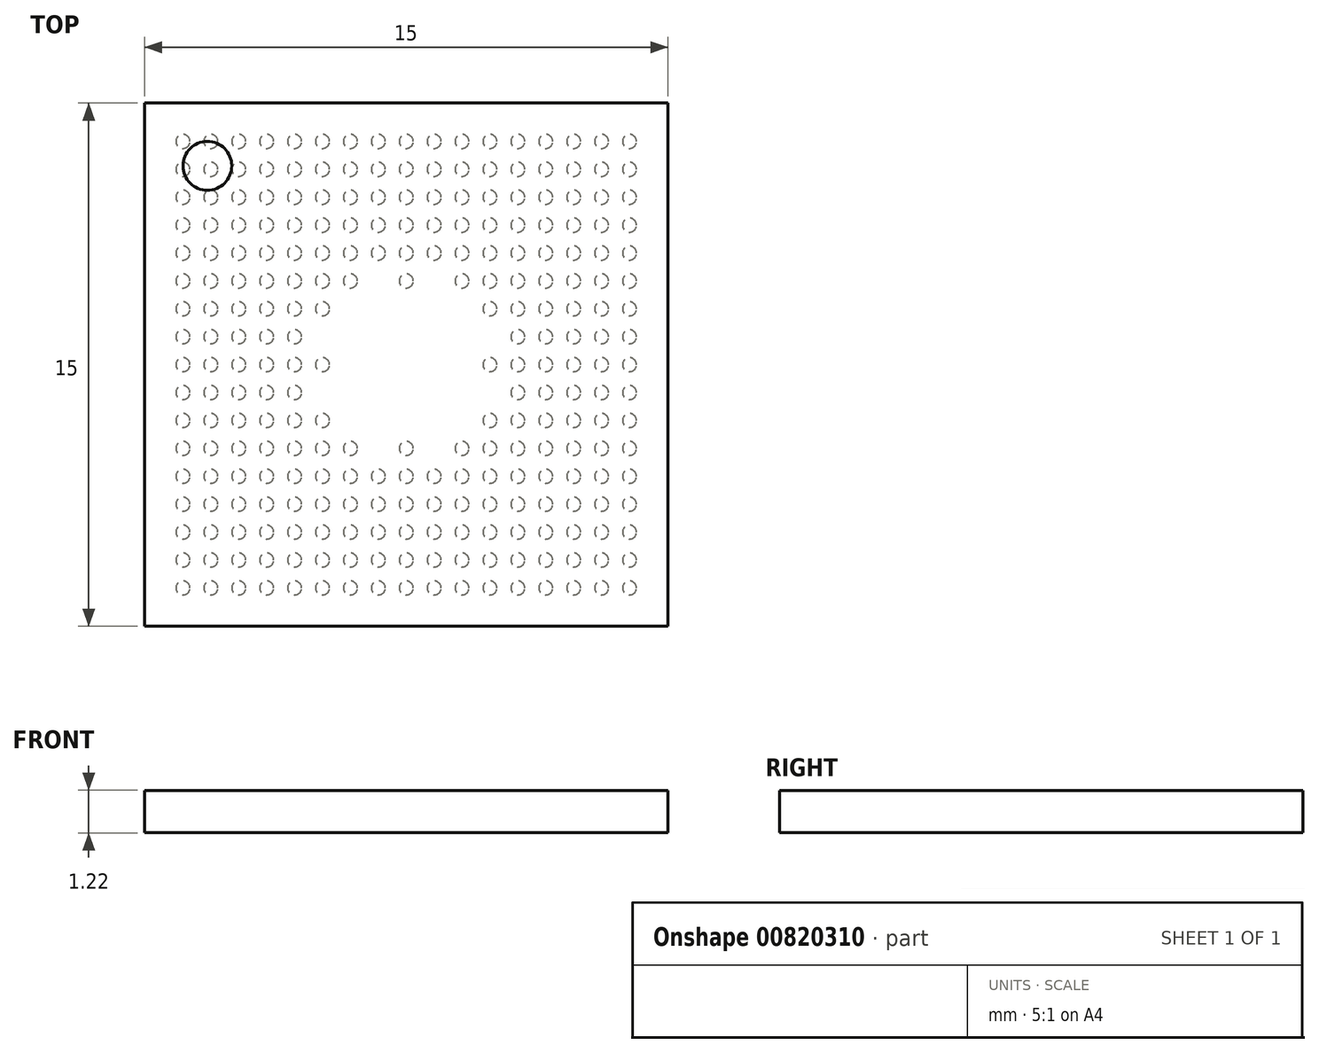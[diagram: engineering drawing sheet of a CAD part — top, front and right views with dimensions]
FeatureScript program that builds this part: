
annotation { "Feature Type Name" : "Feature", "Feature Type Description" : "" }
export const myFeature = defineFeature(function(context is Context, id is Id, definition is map)
    precondition{}
    {
        {
            var Q0;
            Q0=qCreatedBy(makeId("Top.planeOp"),FACE);
            var sketch = newSketch(context, id + "F0", { "sketchPlane" : qUnion([Q0])});
            skLineSegment(sketch, "E0.bottom", {"start": v(7.5, 7.5) * mm, "end": v(-7.5, 7.5) * mm});
            skLineSegment(sketch, "E0.top", {"start": v(7.5, -7.5) * mm, "end": v(-7.5, -7.5) * mm});
            skLineSegment(sketch, "E0.left", {"start": v(7.5, 7.5) * mm, "end": v(7.5, -7.5) * mm});
            skLineSegment(sketch, "E0.right", {"start": v(-7.5, 7.5) * mm, "end": v(-7.5, -7.5) * mm});
            skPoint(sketch, "E0.middle", {"position": v(0, 0) * mm});
            skSolve(sketch);
        }
        {
            var Q0;
            Q0=makeQuery(id+"F0.imprint","IMPRINT",FACE,{"disambiguationData":[TD([[makeQuery(id+"F0.imprint","IMPRINT",EDGE,{"derivedFrom":sQuery(id+"F0.wireOp",EDGE,"E0.bottom")}),1.0]])]});
            extrude(context, id + "F1", {"entities" : qUnion([Q0]), "depth" : 1.2 * mm, "offsetDistance" : 25 * mm});
        }
        {
            var Q0;
            Q0=makeQuery(id+"F1.opExtrude","CAP_FACE",FACE,{"disambiguationData":[OSD([sQuery(id+"F0.wireOp",EDGE,"E0.bottom"),sQuery(id+"F0.wireOp",EDGE,"E0.top"),sQuery(id+"F0.wireOp",EDGE,"E0.left"),sQuery(id+"F0.wireOp",EDGE,"E0.right")])],"isStart":false});
            var sketch = newSketch(context, id + "F2", { "sketchPlane" : qUnion([Q0])});
            skCircle(sketch, "E1", {"center": v(-5.7, 5.7) * mm, "radius": 0.7 * mm});
            skSolve(sketch);
        }
        {
            var Q0;
            Q0=makeQuery(id+"F2.imprint","IMPRINT",FACE,{"disambiguationData":[TD([[makeQuery(id+"F2.imprint","IMPRINT",EDGE,{"derivedFrom":sQuery(id+"F2.wireOp",EDGE,"E1")}),1.0]])]});
            extrude(context, id + "F3", {"entities" : qUnion([Q0]), "endBound" : BoundingType.SYMMETRIC, "depth" : 0.01 * mm, "offsetDistance" : 25 * mm});
        }
        {
            var Q0;
            Q0=makeQuery(id+"F0.imprint","IMPRINT",FACE,{"disambiguationData":[TD([[makeQuery(id+"F0.imprint","IMPRINT",EDGE,{"derivedFrom":sQuery(id+"F0.wireOp",EDGE,"E0.bottom")}),1.0]])]});
            var sketch = newSketch(context, id + "F4", { "sketchPlane" : qUnion([Q0])});
            skCircle(sketch, "E2", {"center": v(0, 0) * mm, "radius": 0.2 * mm});
            skCircle(sketch, "E3", {"center": v(0, -0.8) * mm, "radius": 0.2 * mm});
            skCircle(sketch, "E4", {"center": v(0.8, 0) * mm, "radius": 0.2 * mm});
            skCircle(sketch, "E5", {"center": v(0.8, -0.8) * mm, "radius": 0.2 * mm});
            skCircle(sketch, "E6", {"center": v(1.6, -0.8) * mm, "radius": 0.2 * mm});
            skCircle(sketch, "E7", {"center": v(2.4, -0.8) * mm, "radius": 0.2 * mm});
            skCircle(sketch, "E8", {"center": v(3.2, -0.8) * mm, "radius": 0.2 * mm});
            skCircle(sketch, "E9", {"center": v(4, -0.8) * mm, "radius": 0.2 * mm});
            skCircle(sketch, "E10", {"center": v(4.8, -0.8) * mm, "radius": 0.2 * mm});
            skCircle(sketch, "E11", {"center": v(5.6, -0.8) * mm, "radius": 0.2 * mm});
            skCircle(sketch, "E12", {"center": v(6.4, -0.8) * mm, "radius": 0.2 * mm});
            skCircle(sketch, "E13", {"center": v(1.6, 0) * mm, "radius": 0.2 * mm});
            skCircle(sketch, "E14", {"center": v(2.4, 0) * mm, "radius": 0.2 * mm});
            skCircle(sketch, "E15", {"center": v(3.2, 0) * mm, "radius": 0.2 * mm});
            skCircle(sketch, "E16", {"center": v(4, 0) * mm, "radius": 0.2 * mm});
            skCircle(sketch, "E17", {"center": v(4.8, 0) * mm, "radius": 0.2 * mm});
            skCircle(sketch, "E18", {"center": v(5.6, 0) * mm, "radius": 0.2 * mm});
            skCircle(sketch, "E19", {"center": v(6.4, 0) * mm, "radius": 0.2 * mm});
            skCircle(sketch, "E20.MirrorC", {"center": v(3.2, -1.6) * mm, "radius": 0.2 * mm});
            skCircle(sketch, "E21.MirrorC", {"center": v(2.4, -1.6) * mm, "radius": 0.2 * mm});
            skCircle(sketch, "E22.MirrorC", {"center": v(0.8, -1.6) * mm, "radius": 0.2 * mm});
            skCircle(sketch, "E23.MirrorC", {"center": v(1.6, -1.6) * mm, "radius": 0.2 * mm});
            skCircle(sketch, "E24.MirrorC", {"center": v(4, -1.6) * mm, "radius": 0.2 * mm});
            skCircle(sketch, "E25.MirrorC", {"center": v(0.8, -2.4) * mm, "radius": 0.2 * mm});
            skCircle(sketch, "E26.MirrorC", {"center": v(5.6, -1.6) * mm, "radius": 0.2 * mm});
            skCircle(sketch, "E27.MirrorC", {"center": v(0, -1.6) * mm, "radius": 0.2 * mm});
            skCircle(sketch, "E28.MirrorC", {"center": v(5.6, -2.4) * mm, "radius": 0.2 * mm});
            skCircle(sketch, "E29.MirrorC", {"center": v(0, -2.4) * mm, "radius": 0.2 * mm});
            skCircle(sketch, "E30.MirrorC", {"center": v(4.8, -1.6) * mm, "radius": 0.2 * mm});
            skCircle(sketch, "E31.MirrorC", {"center": v(2.4, -2.4) * mm, "radius": 0.2 * mm});
            skCircle(sketch, "E32.MirrorC", {"center": v(6.4, -1.6) * mm, "radius": 0.2 * mm});
            skCircle(sketch, "E33.MirrorC", {"center": v(1.6, -2.4) * mm, "radius": 0.2 * mm});
            skCircle(sketch, "E34.MirrorC", {"center": v(4.8, -2.4) * mm, "radius": 0.2 * mm});
            skCircle(sketch, "E35.MirrorC", {"center": v(4, -2.4) * mm, "radius": 0.2 * mm});
            skCircle(sketch, "E36.MirrorC", {"center": v(3.2, -2.4) * mm, "radius": 0.2 * mm});
            skCircle(sketch, "E37.MirrorC", {"center": v(6.4, -2.4) * mm, "radius": 0.2 * mm});
            skCircle(sketch, "E38.MirrorC", {"center": v(6.4, -4) * mm, "radius": 0.2 * mm});
            skCircle(sketch, "E39.MirrorC", {"center": v(5.6, -4) * mm, "radius": 0.2 * mm});
            skCircle(sketch, "E40.MirrorC", {"center": v(4.8, -4) * mm, "radius": 0.2 * mm});
            skCircle(sketch, "E41.MirrorC", {"center": v(2.4, -5.6) * mm, "radius": 0.2 * mm});
            skCircle(sketch, "E42.MirrorC", {"center": v(1.6, -5.6) * mm, "radius": 0.2 * mm});
            skCircle(sketch, "E43.MirrorC", {"center": v(3.2, -5.6) * mm, "radius": 0.2 * mm});
            skCircle(sketch, "E44.MirrorC", {"center": v(4, -5.6) * mm, "radius": 0.2 * mm});
            skCircle(sketch, "E45.MirrorC", {"center": v(4.8, -5.6) * mm, "radius": 0.2 * mm});
            skCircle(sketch, "E46.MirrorC", {"center": v(0, -5.6) * mm, "radius": 0.2 * mm});
            skCircle(sketch, "E47.MirrorC", {"center": v(1.6, -4) * mm, "radius": 0.2 * mm});
            skCircle(sketch, "E48.MirrorC", {"center": v(5.6, -5.6) * mm, "radius": 0.2 * mm});
            skCircle(sketch, "E49.MirrorC", {"center": v(0, -4.8) * mm, "radius": 0.2 * mm});
            skCircle(sketch, "E50.MirrorC", {"center": v(2.4, -4) * mm, "radius": 0.2 * mm});
            skCircle(sketch, "E51.MirrorC", {"center": v(4, -4) * mm, "radius": 0.2 * mm});
            skCircle(sketch, "E52.MirrorC", {"center": v(3.2, -4) * mm, "radius": 0.2 * mm});
            skCircle(sketch, "E53.MirrorC", {"center": v(0.8, -5.6) * mm, "radius": 0.2 * mm});
            skCircle(sketch, "E54.MirrorC", {"center": v(0, -4) * mm, "radius": 0.2 * mm});
            skCircle(sketch, "E55.MirrorC", {"center": v(0.8, -4.8) * mm, "radius": 0.2 * mm});
            skCircle(sketch, "E56.MirrorC", {"center": v(1.6, -4.8) * mm, "radius": 0.2 * mm});
            skCircle(sketch, "E57.MirrorC", {"center": v(2.4, -4.8) * mm, "radius": 0.2 * mm});
            skCircle(sketch, "E58.MirrorC", {"center": v(6.4, -5.6) * mm, "radius": 0.2 * mm});
            skCircle(sketch, "E59.MirrorC", {"center": v(0.8, -4) * mm, "radius": 0.2 * mm});
            skCircle(sketch, "E60.MirrorC", {"center": v(3.2, -4.8) * mm, "radius": 0.2 * mm});
            skCircle(sketch, "E61.MirrorC", {"center": v(6.4, -4.8) * mm, "radius": 0.2 * mm});
            skCircle(sketch, "E62.MirrorC", {"center": v(5.6, -4.8) * mm, "radius": 0.2 * mm});
            skCircle(sketch, "E63.MirrorC", {"center": v(4.8, -4.8) * mm, "radius": 0.2 * mm});
            skCircle(sketch, "E64.MirrorC", {"center": v(4, -4.8) * mm, "radius": 0.2 * mm});
            skCircle(sketch, "E65.MirrorC", {"center": v(0, -3.2) * mm, "radius": 0.2 * mm});
            skCircle(sketch, "E66.MirrorC", {"center": v(0.8, -3.2) * mm, "radius": 0.2 * mm});
            skCircle(sketch, "E67.MirrorC", {"center": v(1.6, -3.2) * mm, "radius": 0.2 * mm});
            skCircle(sketch, "E68.MirrorC", {"center": v(2.4, -3.2) * mm, "radius": 0.2 * mm});
            skCircle(sketch, "E69.MirrorC", {"center": v(3.2, -3.2) * mm, "radius": 0.2 * mm});
            skCircle(sketch, "E70.MirrorC", {"center": v(4, -3.2) * mm, "radius": 0.2 * mm});
            skCircle(sketch, "E71.MirrorC", {"center": v(4.8, -3.2) * mm, "radius": 0.2 * mm});
            skCircle(sketch, "E72.MirrorC", {"center": v(5.6, -3.2) * mm, "radius": 0.2 * mm});
            skCircle(sketch, "E73.MirrorC", {"center": v(6.4, -3.2) * mm, "radius": 0.2 * mm});
            skCircle(sketch, "E74.MirrorC", {"center": v(5.6, -6.4) * mm, "radius": 0.2 * mm});
            skCircle(sketch, "E75.MirrorC", {"center": v(0, -6.4) * mm, "radius": 0.2 * mm});
            skCircle(sketch, "E76.MirrorC", {"center": v(2.4, -6.4) * mm, "radius": 0.2 * mm});
            skCircle(sketch, "E77.MirrorC", {"center": v(1.6, -6.4) * mm, "radius": 0.2 * mm});
            skCircle(sketch, "E78.MirrorC", {"center": v(6.4, -6.4) * mm, "radius": 0.2 * mm});
            skCircle(sketch, "E79.MirrorC", {"center": v(3.2, -6.4) * mm, "radius": 0.2 * mm});
            skCircle(sketch, "E80.MirrorC", {"center": v(4.8, -6.4) * mm, "radius": 0.2 * mm});
            skCircle(sketch, "E81.MirrorC", {"center": v(0.8, -6.4) * mm, "radius": 0.2 * mm});
            skCircle(sketch, "E82.MirrorC", {"center": v(4, -6.4) * mm, "radius": 0.2 * mm});
            skCircle(sketch, "E83.MirrorC", {"center": v(-1.6, -4.8) * mm, "radius": 0.2 * mm});
            skCircle(sketch, "E84.MirrorC", {"center": v(-1.6, -2.4) * mm, "radius": 0.2 * mm});
            skCircle(sketch, "E85.MirrorC", {"center": v(-4, -1.6) * mm, "radius": 0.2 * mm});
            skCircle(sketch, "E86.MirrorC", {"center": v(-4.8, -4) * mm, "radius": 0.2 * mm});
            skCircle(sketch, "E87.MirrorC", {"center": v(-0.8, -6.4) * mm, "radius": 0.2 * mm});
            skCircle(sketch, "E88.MirrorC", {"center": v(-5.6, -3.2) * mm, "radius": 0.2 * mm});
            skCircle(sketch, "E89.MirrorC", {"center": v(-2.4, -4) * mm, "radius": 0.2 * mm});
            skCircle(sketch, "E90.MirrorC", {"center": v(-4.8, -2.4) * mm, "radius": 0.2 * mm});
            skCircle(sketch, "E91.MirrorC", {"center": v(-4.8, -3.2) * mm, "radius": 0.2 * mm});
            skCircle(sketch, "E92.MirrorC", {"center": v(-5.6, 0) * mm, "radius": 0.2 * mm});
            skCircle(sketch, "E93.MirrorC", {"center": v(-4.8, -6.4) * mm, "radius": 0.2 * mm});
            skCircle(sketch, "E94.MirrorC", {"center": v(-4, -4.8) * mm, "radius": 0.2 * mm});
            skCircle(sketch, "E95.MirrorC", {"center": v(-1.6, -1.6) * mm, "radius": 0.2 * mm});
            skCircle(sketch, "E96.MirrorC", {"center": v(-5.6, -4) * mm, "radius": 0.2 * mm});
            skCircle(sketch, "E97.MirrorC", {"center": v(-6.4, -1.6) * mm, "radius": 0.2 * mm});
            skCircle(sketch, "E98.MirrorC", {"center": v(-6.4, -3.2) * mm, "radius": 0.2 * mm});
            skCircle(sketch, "E99.MirrorC", {"center": v(-5.6, -1.6) * mm, "radius": 0.2 * mm});
            skCircle(sketch, "E100.MirrorC", {"center": v(-2.4, -5.6) * mm, "radius": 0.2 * mm});
            skCircle(sketch, "E101.MirrorC", {"center": v(-2.4, -4.8) * mm, "radius": 0.2 * mm});
            skCircle(sketch, "E102.MirrorC", {"center": v(-1.6, -3.2) * mm, "radius": 0.2 * mm});
            skCircle(sketch, "E103.MirrorC", {"center": v(-5.6, -6.4) * mm, "radius": 0.2 * mm});
            skCircle(sketch, "E104.MirrorC", {"center": v(-6.4, -5.6) * mm, "radius": 0.2 * mm});
            skCircle(sketch, "E105.MirrorC", {"center": v(-1.6, -5.6) * mm, "radius": 0.2 * mm});
            skCircle(sketch, "E106.MirrorC", {"center": v(-4, -4) * mm, "radius": 0.2 * mm});
            skCircle(sketch, "E107.MirrorC", {"center": v(-4, -2.4) * mm, "radius": 0.2 * mm});
            skCircle(sketch, "E108.MirrorC", {"center": v(-6.4, 0) * mm, "radius": 0.2 * mm});
            skCircle(sketch, "E109.MirrorC", {"center": v(-0.8, -4) * mm, "radius": 0.2 * mm});
            skCircle(sketch, "E110.MirrorC", {"center": v(-3.2, -5.6) * mm, "radius": 0.2 * mm});
            skCircle(sketch, "E111.MirrorC", {"center": v(-3.2, -4) * mm, "radius": 0.2 * mm});
            skCircle(sketch, "E112.MirrorC", {"center": v(-3.2, -2.4) * mm, "radius": 0.2 * mm});
            skCircle(sketch, "E113.MirrorC", {"center": v(-3.2, -1.6) * mm, "radius": 0.2 * mm});
            skCircle(sketch, "E114.MirrorC", {"center": v(-2.4, -3.2) * mm, "radius": 0.2 * mm});
            skCircle(sketch, "E115.MirrorC", {"center": v(-0.8, -3.2) * mm, "radius": 0.2 * mm});
            skCircle(sketch, "E116.MirrorC", {"center": v(-5.6, -2.4) * mm, "radius": 0.2 * mm});
            skCircle(sketch, "E117.MirrorC", {"center": v(-2.4, -6.4) * mm, "radius": 0.2 * mm});
            skCircle(sketch, "E118.MirrorC", {"center": v(-4, -5.6) * mm, "radius": 0.2 * mm});
            skCircle(sketch, "E119.MirrorC", {"center": v(-3.2, -4.8) * mm, "radius": 0.2 * mm});
            skCircle(sketch, "E120.MirrorC", {"center": v(-0.8, -5.6) * mm, "radius": 0.2 * mm});
            skCircle(sketch, "E121.MirrorC", {"center": v(-6.4, -2.4) * mm, "radius": 0.2 * mm});
            skCircle(sketch, "E122.MirrorC", {"center": v(-2.4, -1.6) * mm, "radius": 0.2 * mm});
            skCircle(sketch, "E123.MirrorC", {"center": v(-3.2, -3.2) * mm, "radius": 0.2 * mm});
            skCircle(sketch, "E124.MirrorC", {"center": v(-6.4, -6.4) * mm, "radius": 0.2 * mm});
            skCircle(sketch, "E125.MirrorC", {"center": v(-0.8, -4.8) * mm, "radius": 0.2 * mm});
            skCircle(sketch, "E126.MirrorC", {"center": v(-4, 0) * mm, "radius": 0.2 * mm});
            skCircle(sketch, "E127.MirrorC", {"center": v(-5.6, -4.8) * mm, "radius": 0.2 * mm});
            skCircle(sketch, "E128.MirrorC", {"center": v(-4.8, -1.6) * mm, "radius": 0.2 * mm});
            skCircle(sketch, "E129.MirrorC", {"center": v(-4.8, 0) * mm, "radius": 0.2 * mm});
            skCircle(sketch, "E130.MirrorC", {"center": v(-4.8, -0.8) * mm, "radius": 0.2 * mm});
            skCircle(sketch, "E131.MirrorC", {"center": v(-5.6, -0.8) * mm, "radius": 0.2 * mm});
            skCircle(sketch, "E132.MirrorC", {"center": v(-0.8, -2.4) * mm, "radius": 0.2 * mm});
            skCircle(sketch, "E133.MirrorC", {"center": v(-6.4, -4.8) * mm, "radius": 0.2 * mm});
            skCircle(sketch, "E134.MirrorC", {"center": v(-4, -0.8) * mm, "radius": 0.2 * mm});
            skCircle(sketch, "E135.MirrorC", {"center": v(-6.4, -0.8) * mm, "radius": 0.2 * mm});
            skCircle(sketch, "E136.MirrorC", {"center": v(-5.6, -5.6) * mm, "radius": 0.2 * mm});
            skCircle(sketch, "E137.MirrorC", {"center": v(-1.6, -4) * mm, "radius": 0.2 * mm});
            skCircle(sketch, "E138.MirrorC", {"center": v(-3.2, -0.8) * mm, "radius": 0.2 * mm});
            skCircle(sketch, "E139.MirrorC", {"center": v(-2.4, -0.8) * mm, "radius": 0.2 * mm});
            skCircle(sketch, "E140.MirrorC", {"center": v(-4.8, -5.6) * mm, "radius": 0.2 * mm});
            skCircle(sketch, "E141.MirrorC", {"center": v(-0.8, -0.8) * mm, "radius": 0.2 * mm});
            skCircle(sketch, "E142.MirrorC", {"center": v(-1.6, -0.8) * mm, "radius": 0.2 * mm});
            skCircle(sketch, "E143.MirrorC", {"center": v(-1.6, -6.4) * mm, "radius": 0.2 * mm});
            skCircle(sketch, "E144.MirrorC", {"center": v(-0.8, 0) * mm, "radius": 0.2 * mm});
            skCircle(sketch, "E145.MirrorC", {"center": v(-2.4, -2.4) * mm, "radius": 0.2 * mm});
            skCircle(sketch, "E146.MirrorC", {"center": v(-6.4, -4) * mm, "radius": 0.2 * mm});
            skCircle(sketch, "E147.MirrorC", {"center": v(-0.8, -1.6) * mm, "radius": 0.2 * mm});
            skCircle(sketch, "E148.MirrorC", {"center": v(-4, -6.4) * mm, "radius": 0.2 * mm});
            skCircle(sketch, "E149.MirrorC", {"center": v(-4, -3.2) * mm, "radius": 0.2 * mm});
            skCircle(sketch, "E150.MirrorC", {"center": v(-1.6, 0) * mm, "radius": 0.2 * mm});
            skCircle(sketch, "E151.MirrorC", {"center": v(-3.2, 0) * mm, "radius": 0.2 * mm});
            skCircle(sketch, "E152.MirrorC", {"center": v(-2.4, 0) * mm, "radius": 0.2 * mm});
            skCircle(sketch, "E153.MirrorC", {"center": v(-4.8, -4.8) * mm, "radius": 0.2 * mm});
            skCircle(sketch, "E154.MirrorC", {"center": v(-3.2, -6.4) * mm, "radius": 0.2 * mm});
            skCircle(sketch, "E155.MirrorC", {"center": v(0, 4) * mm, "radius": 0.2 * mm});
            skCircle(sketch, "E156.MirrorC", {"center": v(0, 4.8) * mm, "radius": 0.2 * mm});
            skCircle(sketch, "E157.MirrorC", {"center": v(0, 5.6) * mm, "radius": 0.2 * mm});
            skCircle(sketch, "E158.MirrorC", {"center": v(0, 0.8) * mm, "radius": 0.2 * mm});
            skCircle(sketch, "E159.MirrorC", {"center": v(0, 6.4) * mm, "radius": 0.2 * mm});
            skCircle(sketch, "E160.MirrorC", {"center": v(0, 1.6) * mm, "radius": 0.2 * mm});
            skCircle(sketch, "E161.MirrorC", {"center": v(0, 3.2) * mm, "radius": 0.2 * mm});
            skCircle(sketch, "E162.MirrorC", {"center": v(0, 2.4) * mm, "radius": 0.2 * mm});
            skCircle(sketch, "E163.MirrorC", {"center": v(4.8, 3.2) * mm, "radius": 0.2 * mm});
            skCircle(sketch, "E164.MirrorC", {"center": v(-4.8, 4) * mm, "radius": 0.2 * mm});
            skCircle(sketch, "E165.MirrorC", {"center": v(-2.4, 4.8) * mm, "radius": 0.2 * mm});
            skCircle(sketch, "E166.MirrorC", {"center": v(-0.8, 3.2) * mm, "radius": 0.2 * mm});
            skCircle(sketch, "E167.MirrorC", {"center": v(1.6, 1.6) * mm, "radius": 0.2 * mm});
            skCircle(sketch, "E168.MirrorC", {"center": v(5.6, 4) * mm, "radius": 0.2 * mm});
            skCircle(sketch, "E169.MirrorC", {"center": v(0.8, 4.8) * mm, "radius": 0.2 * mm});
            skCircle(sketch, "E170.MirrorC", {"center": v(-4.8, 1.6) * mm, "radius": 0.2 * mm});
            skCircle(sketch, "E171.MirrorC", {"center": v(4, 3.2) * mm, "radius": 0.2 * mm});
            skCircle(sketch, "E172.MirrorC", {"center": v(-4, 1.6) * mm, "radius": 0.2 * mm});
            skCircle(sketch, "E173.MirrorC", {"center": v(-2.4, 5.6) * mm, "radius": 0.2 * mm});
            skCircle(sketch, "E174.MirrorC", {"center": v(-2.4, 3.2) * mm, "radius": 0.2 * mm});
            skCircle(sketch, "E175.MirrorC", {"center": v(0.8, 1.6) * mm, "radius": 0.2 * mm});
            skCircle(sketch, "E176.MirrorC", {"center": v(6.4, 4) * mm, "radius": 0.2 * mm});
            skCircle(sketch, "E177.MirrorC", {"center": v(6.4, 0.8) * mm, "radius": 0.2 * mm});
            skCircle(sketch, "E178.MirrorC", {"center": v(5.6, 0.8) * mm, "radius": 0.2 * mm});
            skCircle(sketch, "E179.MirrorC", {"center": v(4.8, 0.8) * mm, "radius": 0.2 * mm});
            skCircle(sketch, "E180.MirrorC", {"center": v(4, 0.8) * mm, "radius": 0.2 * mm});
            skCircle(sketch, "E181.MirrorC", {"center": v(3.2, 0.8) * mm, "radius": 0.2 * mm});
            skCircle(sketch, "E182.MirrorC", {"center": v(2.4, 0.8) * mm, "radius": 0.2 * mm});
            skCircle(sketch, "E183.MirrorC", {"center": v(1.6, 0.8) * mm, "radius": 0.2 * mm});
            skCircle(sketch, "E184.MirrorC", {"center": v(0.8, 0.8) * mm, "radius": 0.2 * mm});
            skCircle(sketch, "E185.MirrorC", {"center": v(-5.6, 4.8) * mm, "radius": 0.2 * mm});
            skCircle(sketch, "E186.MirrorC", {"center": v(-1.6, 6.4) * mm, "radius": 0.2 * mm});
            skCircle(sketch, "E187.MirrorC", {"center": v(3.2, 3.2) * mm, "radius": 0.2 * mm});
            skCircle(sketch, "E188.MirrorC", {"center": v(-1.6, 2.4) * mm, "radius": 0.2 * mm});
            skCircle(sketch, "E189.MirrorC", {"center": v(-5.6, 1.6) * mm, "radius": 0.2 * mm});
            skCircle(sketch, "E190.MirrorC", {"center": v(-3.2, 1.6) * mm, "radius": 0.2 * mm});
            skCircle(sketch, "E191.MirrorC", {"center": v(2.4, 1.6) * mm, "radius": 0.2 * mm});
            skCircle(sketch, "E192.MirrorC", {"center": v(6.4, 2.4) * mm, "radius": 0.2 * mm});
            skCircle(sketch, "E193.MirrorC", {"center": v(0.8, 5.6) * mm, "radius": 0.2 * mm});
            skCircle(sketch, "E194.MirrorC", {"center": v(2.4, 3.2) * mm, "radius": 0.2 * mm});
            skCircle(sketch, "E195.MirrorC", {"center": v(-1.6, 4.8) * mm, "radius": 0.2 * mm});
            skCircle(sketch, "E196.MirrorC", {"center": v(-6.4, 3.2) * mm, "radius": 0.2 * mm});
            skCircle(sketch, "E197.MirrorC", {"center": v(-3.2, 2.4) * mm, "radius": 0.2 * mm});
            skCircle(sketch, "E198.MirrorC", {"center": v(3.2, 1.6) * mm, "radius": 0.2 * mm});
            skCircle(sketch, "E199.MirrorC", {"center": v(3.2, 2.4) * mm, "radius": 0.2 * mm});
            skCircle(sketch, "E200.MirrorC", {"center": v(3.2, 4) * mm, "radius": 0.2 * mm});
            skCircle(sketch, "E201.MirrorC", {"center": v(-1.6, 0.8) * mm, "radius": 0.2 * mm});
            skCircle(sketch, "E202.MirrorC", {"center": v(4, 2.4) * mm, "radius": 0.2 * mm});
            skCircle(sketch, "E203.MirrorC", {"center": v(4, 4) * mm, "radius": 0.2 * mm});
            skCircle(sketch, "E204.MirrorC", {"center": v(-0.8, 0.8) * mm, "radius": 0.2 * mm});
            skCircle(sketch, "E205.MirrorC", {"center": v(-3.2, 6.4) * mm, "radius": 0.2 * mm});
            skCircle(sketch, "E206.MirrorC", {"center": v(1.6, 3.2) * mm, "radius": 0.2 * mm});
            skCircle(sketch, "E207.MirrorC", {"center": v(-6.4, 1.6) * mm, "radius": 0.2 * mm});
            skCircle(sketch, "E208.MirrorC", {"center": v(-3.2, 4) * mm, "radius": 0.2 * mm});
            skCircle(sketch, "E209.MirrorC", {"center": v(-4.8, 5.6) * mm, "radius": 0.2 * mm});
            skCircle(sketch, "E210.MirrorC", {"center": v(-4.8, 4.8) * mm, "radius": 0.2 * mm});
            skCircle(sketch, "E211.MirrorC", {"center": v(0.8, 3.2) * mm, "radius": 0.2 * mm});
            skCircle(sketch, "E212.MirrorC", {"center": v(4, 6.4) * mm, "radius": 0.2 * mm});
            skCircle(sketch, "E213.MirrorC", {"center": v(-5.6, 4) * mm, "radius": 0.2 * mm});
            skCircle(sketch, "E214.MirrorC", {"center": v(-3.2, 5.6) * mm, "radius": 0.2 * mm});
            skCircle(sketch, "E215.MirrorC", {"center": v(4.8, 2.4) * mm, "radius": 0.2 * mm});
            skCircle(sketch, "E216.MirrorC", {"center": v(-0.8, 4.8) * mm, "radius": 0.2 * mm});
            skCircle(sketch, "E217.MirrorC", {"center": v(-2.4, 0.8) * mm, "radius": 0.2 * mm});
            skCircle(sketch, "E218.MirrorC", {"center": v(2.4, 4) * mm, "radius": 0.2 * mm});
            skCircle(sketch, "E219.MirrorC", {"center": v(-4.8, 3.2) * mm, "radius": 0.2 * mm});
            skCircle(sketch, "E220.MirrorC", {"center": v(1.6, 2.4) * mm, "radius": 0.2 * mm});
            skCircle(sketch, "E221.MirrorC", {"center": v(1.6, 6.4) * mm, "radius": 0.2 * mm});
            skCircle(sketch, "E222.MirrorC", {"center": v(6.4, 4.8) * mm, "radius": 0.2 * mm});
            skCircle(sketch, "E223.MirrorC", {"center": v(-4, 6.4) * mm, "radius": 0.2 * mm});
            skCircle(sketch, "E224.MirrorC", {"center": v(4.8, 5.6) * mm, "radius": 0.2 * mm});
            skCircle(sketch, "E225.MirrorC", {"center": v(-4, 4) * mm, "radius": 0.2 * mm});
            skCircle(sketch, "E226.MirrorC", {"center": v(-0.8, 5.6) * mm, "radius": 0.2 * mm});
            skCircle(sketch, "E227.MirrorC", {"center": v(-4, 0.8) * mm, "radius": 0.2 * mm});
            skCircle(sketch, "E228.MirrorC", {"center": v(-3.2, 0.8) * mm, "radius": 0.2 * mm});
            skCircle(sketch, "E229.MirrorC", {"center": v(-6.4, 6.4) * mm, "radius": 0.2 * mm});
            skCircle(sketch, "E230.MirrorC", {"center": v(-0.8, 1.6) * mm, "radius": 0.2 * mm});
            skCircle(sketch, "E231.MirrorC", {"center": v(4, 4.8) * mm, "radius": 0.2 * mm});
            skCircle(sketch, "E232.MirrorC", {"center": v(3.2, 4.8) * mm, "radius": 0.2 * mm});
            skCircle(sketch, "E233.MirrorC", {"center": v(-4.8, 2.4) * mm, "radius": 0.2 * mm});
            skCircle(sketch, "E234.MirrorC", {"center": v(4, 5.6) * mm, "radius": 0.2 * mm});
            skCircle(sketch, "E235.MirrorC", {"center": v(4.8, 6.4) * mm, "radius": 0.2 * mm});
            skCircle(sketch, "E236.MirrorC", {"center": v(2.4, 6.4) * mm, "radius": 0.2 * mm});
            skCircle(sketch, "E237.MirrorC", {"center": v(-4, 4.8) * mm, "radius": 0.2 * mm});
            skCircle(sketch, "E238.MirrorC", {"center": v(5.6, 2.4) * mm, "radius": 0.2 * mm});
            skCircle(sketch, "E239.MirrorC", {"center": v(6.4, 1.6) * mm, "radius": 0.2 * mm});
            skCircle(sketch, "E240.MirrorC", {"center": v(5.6, 5.6) * mm, "radius": 0.2 * mm});
            skCircle(sketch, "E241.MirrorC", {"center": v(-2.4, 1.6) * mm, "radius": 0.2 * mm});
            skCircle(sketch, "E242.MirrorC", {"center": v(-4, 3.2) * mm, "radius": 0.2 * mm});
            skCircle(sketch, "E243.MirrorC", {"center": v(-5.6, 5.6) * mm, "radius": 0.2 * mm});
            skCircle(sketch, "E244.MirrorC", {"center": v(-1.6, 5.6) * mm, "radius": 0.2 * mm});
            skCircle(sketch, "E245.MirrorC", {"center": v(-3.2, 4.8) * mm, "radius": 0.2 * mm});
            skCircle(sketch, "E246.MirrorC", {"center": v(-6.4, 4.8) * mm, "radius": 0.2 * mm});
            skCircle(sketch, "E247.MirrorC", {"center": v(5.6, 4.8) * mm, "radius": 0.2 * mm});
            skCircle(sketch, "E248.MirrorC", {"center": v(6.4, 6.4) * mm, "radius": 0.2 * mm});
            skCircle(sketch, "E249.MirrorC", {"center": v(4.8, 1.6) * mm, "radius": 0.2 * mm});
            skCircle(sketch, "E250.MirrorC", {"center": v(0.8, 4) * mm, "radius": 0.2 * mm});
            skCircle(sketch, "E251.MirrorC", {"center": v(-2.4, 4) * mm, "radius": 0.2 * mm});
            skCircle(sketch, "E252.MirrorC", {"center": v(3.2, 5.6) * mm, "radius": 0.2 * mm});
            skCircle(sketch, "E253.MirrorC", {"center": v(-6.4, 5.6) * mm, "radius": 0.2 * mm});
            skCircle(sketch, "E254.MirrorC", {"center": v(-4, 5.6) * mm, "radius": 0.2 * mm});
            skCircle(sketch, "E255.MirrorC", {"center": v(1.6, 4) * mm, "radius": 0.2 * mm});
            skCircle(sketch, "E256.MirrorC", {"center": v(-4, 2.4) * mm, "radius": 0.2 * mm});
            skCircle(sketch, "E257.MirrorC", {"center": v(4.8, 4) * mm, "radius": 0.2 * mm});
            skCircle(sketch, "E258.MirrorC", {"center": v(2.4, 2.4) * mm, "radius": 0.2 * mm});
            skCircle(sketch, "E259.MirrorC", {"center": v(4, 1.6) * mm, "radius": 0.2 * mm});
            skCircle(sketch, "E260.MirrorC", {"center": v(-5.6, 2.4) * mm, "radius": 0.2 * mm});
            skCircle(sketch, "E261.MirrorC", {"center": v(1.6, 4.8) * mm, "radius": 0.2 * mm});
            skCircle(sketch, "E262.MirrorC", {"center": v(-1.6, 3.2) * mm, "radius": 0.2 * mm});
            skCircle(sketch, "E263.MirrorC", {"center": v(-0.8, 6.4) * mm, "radius": 0.2 * mm});
            skCircle(sketch, "E264.MirrorC", {"center": v(-0.8, 4) * mm, "radius": 0.2 * mm});
            skCircle(sketch, "E265.MirrorC", {"center": v(6.4, 3.2) * mm, "radius": 0.2 * mm});
            skCircle(sketch, "E266.MirrorC", {"center": v(-2.4, 2.4) * mm, "radius": 0.2 * mm});
            skCircle(sketch, "E267.MirrorC", {"center": v(2.4, 4.8) * mm, "radius": 0.2 * mm});
            skCircle(sketch, "E268.MirrorC", {"center": v(2.4, 5.6) * mm, "radius": 0.2 * mm});
            skCircle(sketch, "E269.MirrorC", {"center": v(0.8, 6.4) * mm, "radius": 0.2 * mm});
            skCircle(sketch, "E270.MirrorC", {"center": v(-5.6, 6.4) * mm, "radius": 0.2 * mm});
            skCircle(sketch, "E271.MirrorC", {"center": v(-5.6, 0.8) * mm, "radius": 0.2 * mm});
            skCircle(sketch, "E272.MirrorC", {"center": v(-6.4, 2.4) * mm, "radius": 0.2 * mm});
            skCircle(sketch, "E273.MirrorC", {"center": v(-6.4, 4) * mm, "radius": 0.2 * mm});
            skCircle(sketch, "E274.MirrorC", {"center": v(-3.2, 3.2) * mm, "radius": 0.2 * mm});
            skCircle(sketch, "E275.MirrorC", {"center": v(-2.4, 6.4) * mm, "radius": 0.2 * mm});
            skCircle(sketch, "E276.MirrorC", {"center": v(-0.8, 2.4) * mm, "radius": 0.2 * mm});
            skCircle(sketch, "E277.MirrorC", {"center": v(6.4, 5.6) * mm, "radius": 0.2 * mm});
            skCircle(sketch, "E278.MirrorC", {"center": v(-5.6, 3.2) * mm, "radius": 0.2 * mm});
            skCircle(sketch, "E279.MirrorC", {"center": v(5.6, 1.6) * mm, "radius": 0.2 * mm});
            skCircle(sketch, "E280.MirrorC", {"center": v(5.6, 6.4) * mm, "radius": 0.2 * mm});
            skCircle(sketch, "E281.MirrorC", {"center": v(-1.6, 4) * mm, "radius": 0.2 * mm});
            skCircle(sketch, "E282.MirrorC", {"center": v(1.6, 5.6) * mm, "radius": 0.2 * mm});
            skCircle(sketch, "E283.MirrorC", {"center": v(0.8, 2.4) * mm, "radius": 0.2 * mm});
            skCircle(sketch, "E284.MirrorC", {"center": v(-4.8, 0.8) * mm, "radius": 0.2 * mm});
            skCircle(sketch, "E285.MirrorC", {"center": v(-4.8, 6.4) * mm, "radius": 0.2 * mm});
            skCircle(sketch, "E286.MirrorC", {"center": v(5.6, 3.2) * mm, "radius": 0.2 * mm});
            skCircle(sketch, "E287.MirrorC", {"center": v(4.8, 4.8) * mm, "radius": 0.2 * mm});
            skCircle(sketch, "E288.MirrorC", {"center": v(-6.4, 0.8) * mm, "radius": 0.2 * mm});
            skCircle(sketch, "E289.MirrorC", {"center": v(-1.6, 1.6) * mm, "radius": 0.2 * mm});
            skCircle(sketch, "E290.MirrorC", {"center": v(3.2, 6.4) * mm, "radius": 0.2 * mm});
            skSolve(sketch);
        }
        {
            var Q0;
            Q0 = qSketchRegion(id + "F4", true);
            extrude(context, id + "F5", {"entities" : qUnion([Q0]), "endBound" : BoundingType.SYMMETRIC, "depth" : 0.01 * mm, "offsetDistance" : 25 * mm});
        }
        {
            var Q0;
            Q0=makeQuery(id+"F5.opExtrude","SWEPT_BODY",BODY,{"disambiguationData":[OSD([sQuery(id+"F4.wireOp",EDGE,"E2")])]});
            var Q1;
            Q1=makeQuery(id+"F5.opExtrude","SWEPT_BODY",BODY,{"disambiguationData":[OSD([sQuery(id+"F4.wireOp",EDGE,"E5")])]});
            var Q2;
            Q2=makeQuery(id+"F5.opExtrude","SWEPT_BODY",BODY,{"disambiguationData":[OSD([sQuery(id+"F4.wireOp",EDGE,"E22.MirrorC")])]});
            var Q3;
            Q3=makeQuery(id+"F5.opExtrude","SWEPT_BODY",BODY,{"disambiguationData":[OSD([sQuery(id+"F4.wireOp",EDGE,"E141.MirrorC")])]});
            var Q4;
            Q4=makeQuery(id+"F5.opExtrude","SWEPT_BODY",BODY,{"disambiguationData":[OSD([sQuery(id+"F4.wireOp",EDGE,"E144.MirrorC")])]});
            var Q5;
            Q5=makeQuery(id+"F5.opExtrude","SWEPT_BODY",BODY,{"disambiguationData":[OSD([sQuery(id+"F4.wireOp",EDGE,"E204.MirrorC")])]});
            var Q6;
            Q6=makeQuery(id+"F5.opExtrude","SWEPT_BODY",BODY,{"disambiguationData":[OSD([sQuery(id+"F4.wireOp",EDGE,"E160.MirrorC")])]});
            var Q7;
            Q7=makeQuery(id+"F5.opExtrude","SWEPT_BODY",BODY,{"disambiguationData":[OSD([sQuery(id+"F4.wireOp",EDGE,"E6")])]});
            var Q8;
            Q8=makeQuery(id+"F5.opExtrude","SWEPT_BODY",BODY,{"disambiguationData":[OSD([sQuery(id+"F4.wireOp",EDGE,"E23.MirrorC")])]});
            var Q9;
            Q9=makeQuery(id+"F5.opExtrude","SWEPT_BODY",BODY,{"disambiguationData":[OSD([sQuery(id+"F4.wireOp",EDGE,"E95.MirrorC")])]});
            var Q10;
            Q10=makeQuery(id+"F5.opExtrude","SWEPT_BODY",BODY,{"disambiguationData":[OSD([sQuery(id+"F4.wireOp",EDGE,"E142.MirrorC")])]});
            var Q11;
            Q11=makeQuery(id+"F5.opExtrude","SWEPT_BODY",BODY,{"disambiguationData":[OSD([sQuery(id+"F4.wireOp",EDGE,"E201.MirrorC")])]});
            var Q12;
            Q12=makeQuery(id+"F5.opExtrude","SWEPT_BODY",BODY,{"disambiguationData":[OSD([sQuery(id+"F4.wireOp",EDGE,"E230.MirrorC")])]});
            var Q13;
            Q13=makeQuery(id+"F5.opExtrude","SWEPT_BODY",BODY,{"disambiguationData":[OSD([sQuery(id+"F4.wireOp",EDGE,"E150.MirrorC")])]});
            var Q14;
            Q14=makeQuery(id+"F5.opExtrude","SWEPT_BODY",BODY,{"disambiguationData":[OSD([sQuery(id+"F4.wireOp",EDGE,"E183.MirrorC")])]});
            deleteBodies(context, id + "F6", {"entities" : qUnion([Q0, Q1, Q2, Q3, Q4, Q5, Q6, Q7, Q8, Q9, Q10, Q11, Q12, Q13, Q14])});
        }
        {
            var Q0;
            Q0=makeQuery(id+"F5.opExtrude","SWEPT_BODY",BODY,{"disambiguationData":[OSD([sQuery(id+"F4.wireOp",EDGE,"E132.MirrorC")])]});
            var Q1;
            Q1=makeQuery(id+"F5.opExtrude","SWEPT_BODY",BODY,{"disambiguationData":[OSD([sQuery(id+"F4.wireOp",EDGE,"E25.MirrorC")])]});
            var Q2;
            Q2=makeQuery(id+"F5.opExtrude","SWEPT_BODY",BODY,{"disambiguationData":[OSD([sQuery(id+"F4.wireOp",EDGE,"E139.MirrorC")])]});
            var Q3;
            Q3=makeQuery(id+"F5.opExtrude","SWEPT_BODY",BODY,{"disambiguationData":[OSD([sQuery(id+"F4.wireOp",EDGE,"E217.MirrorC")])]});
            var Q4;
            Q4=makeQuery(id+"F5.opExtrude","SWEPT_BODY",BODY,{"disambiguationData":[OSD([sQuery(id+"F4.wireOp",EDGE,"E276.MirrorC")])]});
            var Q5;
            Q5=makeQuery(id+"F5.opExtrude","SWEPT_BODY",BODY,{"disambiguationData":[OSD([sQuery(id+"F4.wireOp",EDGE,"E283.MirrorC")])]});
            var Q6;
            Q6=makeQuery(id+"F5.opExtrude","SWEPT_BODY",BODY,{"disambiguationData":[OSD([sQuery(id+"F4.wireOp",EDGE,"E182.MirrorC")])]});
            var Q7;
            Q7=makeQuery(id+"F5.opExtrude","SWEPT_BODY",BODY,{"disambiguationData":[OSD([sQuery(id+"F4.wireOp",EDGE,"E7")])]});
            deleteBodies(context, id + "F7", {"entities" : qUnion([Q0, Q1, Q2, Q3, Q4, Q5, Q6, Q7])});
        }
        {
            var Q0;
            Q0=makeQuery(id+"F5.opExtrude","SWEPT_BODY",BODY,{"disambiguationData":[OSD([sQuery(id+"F4.wireOp",EDGE,"E175.MirrorC")])]});
            var Q1;
            Q1=makeQuery(id+"F5.opExtrude","SWEPT_BODY",BODY,{"disambiguationData":[OSD([sQuery(id+"F4.wireOp",EDGE,"E167.MirrorC")])]});
            var Q2;
            Q2=makeQuery(id+"F5.opExtrude","SWEPT_BODY",BODY,{"disambiguationData":[OSD([sQuery(id+"F4.wireOp",EDGE,"E13")])]});
            var Q3;
            Q3=makeQuery(id+"F5.opExtrude","SWEPT_BODY",BODY,{"disambiguationData":[OSD([sQuery(id+"F4.wireOp",EDGE,"E184.MirrorC")])]});
            var Q4;
            Q4=makeQuery(id+"F5.opExtrude","SWEPT_BODY",BODY,{"disambiguationData":[OSD([sQuery(id+"F4.wireOp",EDGE,"E3")])]});
            var Q5;
            Q5=makeQuery(id+"F5.opExtrude","SWEPT_BODY",BODY,{"disambiguationData":[OSD([sQuery(id+"F4.wireOp",EDGE,"E4")])]});
            var Q6;
            Q6=makeQuery(id+"F5.opExtrude","SWEPT_BODY",BODY,{"disambiguationData":[OSD([sQuery(id+"F4.wireOp",EDGE,"E158.MirrorC")])]});
            deleteBodies(context, id + "F8", {"entities" : qUnion([Q0, Q1, Q2, Q3, Q4, Q5, Q6])});
        }
        {
            var Q0;
            Q0=makeQuery(id+"F5.opExtrude","SWEPT_BODY",BODY,{"disambiguationData":[OSD([sQuery(id+"F4.wireOp",EDGE,"E147.MirrorC")])]});
            var Q1;
            Q1=makeQuery(id+"F5.opExtrude","SWEPT_BODY",BODY,{"disambiguationData":[OSD([sQuery(id+"F4.wireOp",EDGE,"E289.MirrorC")])]});
            deleteBodies(context, id + "F9", {"entities" : qUnion([Q0, Q1])});
        }
        {
            var Q0;
            Q0=makeQuery(id+"F5.opExtrude","SWEPT_BODY",BODY,{"disambiguationData":[OSD([sQuery(id+"F4.wireOp",EDGE,"E27.MirrorC")])]});
            deleteBodies(context, id + "F10", {"entities" : qUnion([Q0])});
        }
    });
